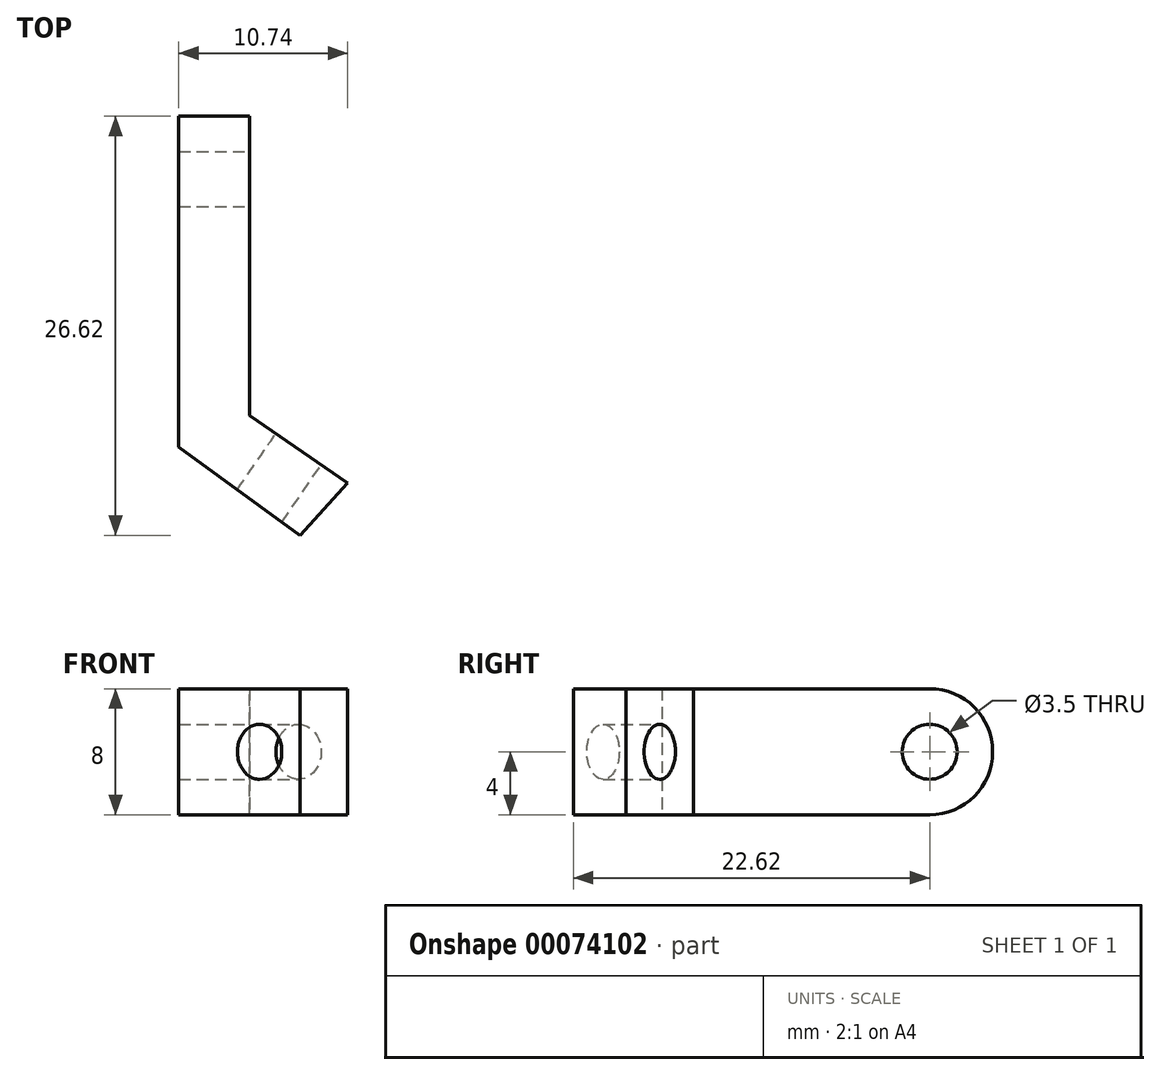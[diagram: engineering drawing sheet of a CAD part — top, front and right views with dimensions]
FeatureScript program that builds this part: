
annotation { "Feature Type Name" : "Feature", "Feature Type Description" : "" }
export const myFeature = defineFeature(function(context is Context, id is Id, definition is map)
    precondition{}
    {
        {
            var Q0;
            Q0=qCreatedBy(makeId("Top.planeOp"),FACE);
            var sketch = newSketch(context, id + "F0", { "sketchPlane" : qUnion([Q0])});
            skLineSegment(sketch, "E0", {"start": v(0, 0) * mm, "end": v(0, -21) * mm});
            skLineSegment(sketch, "E1", {"start": v(0, 0) * mm, "end": v(4.5, 0) * mm});
            skLineSegment(sketch, "E2", {"start": v(4.5, 0) * mm, "end": v(4.5, -19) * mm});
            skLineSegment(sketch, "E3", {"start": v(7.72, -26.62) * mm, "end": v(0, -21) * mm});
            skLineSegment(sketch, "E4", {"start": v(10.74, -23.28) * mm, "end": v(4.5, -19) * mm});
            skLineSegment(sketch, "E5", {"start": v(7.72, -26.62) * mm, "end": v(10.74, -23.28) * mm});
            skSolve(sketch);
        }
        {
            var Q0;
            Q0=makeQuery(id+"F0.imprint","IMPRINT",FACE,{"disambiguationData":[TD([[makeQuery(id+"F0.imprint","IMPRINT",EDGE,{"derivedFrom":sQuery(id+"F0.wireOp",EDGE,"E0")}),1.0]])]});
            var Q1;
            {var subQ3=sQuery(id+"F0.wireOp",EDGE,"l58EZqPc-FLeH-wLxH-H9D7-pOg8m8mRtfT9");Q1=makeQuery(id+"F0.imprint","IMPRINT",FACE,{"disambiguationData":[TD([[makeQuery(id+"F0.imprint","IMPRINT",EDGE,{"derivedFrom":subQ3}),-1.0]])]});}
            extrude(context, id + "F1", {"entities" : qUnion([Q0, Q1]), "depth" : 8 * mm});
        }
        {
            var Q0;
            Q0=makeQuery(id+"F1.opExtrude","CAP_EDGE",EDGE,{"disambiguationData":[OSD([sQuery(id+"F0.wireOp",EDGE,"E1")])],"isStart":false});
            var Q1;
            Q1=makeQuery(id+"F1.opExtrude","CAP_EDGE",EDGE,{"disambiguationData":[OSD([sQuery(id+"F0.wireOp",EDGE,"E1")])],"isStart":true});
            var Q2;
            Q2=makeQuery(id+"F1.opExtrude","CAP_EDGE",EDGE,{"disambiguationData":[OSD([sQuery(id+"F0.wireOp",EDGE,"EgyDUQFE-vDOO-uSj2-E7Fw-uX1ybdiR7PVY")])],"isStart":false});
            var Q3;
            Q3=makeQuery(id+"F1.opExtrude","CAP_EDGE",EDGE,{"disambiguationData":[OSD([sQuery(id+"F0.wireOp",EDGE,"EgyDUQFE-vDOO-uSj2-E7Fw-uX1ybdiR7PVY")])],"isStart":true});
            fillet(context, id + "F2", {"entities" : qUnion([Q0, Q1, Q2, Q3]), "radius" : 4 * mm, "tangentPropagation" : true, "allowEdgeOverflow" : false});
        }
        {
            var Q0;
            Q0=makeQuery(id+"F1.opExtrude","SWEPT_FACE",FACE,{"disambiguationData":[OSD([sQuery(id+"F0.wireOp",EDGE,"E2")])]});
            var sketch = newSketch(context, id + "F3", { "sketchPlane" : qUnion([Q0])});
            skCircle(sketch, "E6", {"center": v(-4, 4) * mm, "radius": 1.75 * mm});
            skSolve(sketch);
        }
        {
            var Q0;
            Q0=makeQuery(id+"F3.imprint","IMPRINT",FACE,{"disambiguationData":[TD([[makeQuery(id+"F3.imprint","IMPRINT",EDGE,{"derivedFrom":sQuery(id+"F3.wireOp",EDGE,"E6")}),1.0]])]});
            extrude(context, id + "F4", {"entities" : qUnion([Q0]), "operationType" : NewBodyOperationType.REMOVE, "oppositeDirection" : true, "depth" : 4.5 * mm});
        }
        {
            var Q0;
            Q0=makeQuery(id+"F1.opExtrude","SWEPT_FACE",FACE,{"disambiguationData":[OSD([sQuery(id+"F0.wireOp",EDGE,"E4")])]});
            var sketch = newSketch(context, id + "F5", { "sketchPlane" : qUnion([Q0])});
            skCircle(sketch, "E7", {"center": v(-18.25, 4) * mm, "radius": 1.75 * mm});
            skSolve(sketch);
        }
        {
            var Q0;
            Q0=makeQuery(id+"F5.imprint","IMPRINT",FACE,{"disambiguationData":[TD([[makeQuery(id+"F5.imprint","IMPRINT",EDGE,{"derivedFrom":sQuery(id+"F5.wireOp",EDGE,"E7")}),1.0]])]});
            extrude(context, id + "F6", {"entities" : qUnion([Q0]), "operationType" : NewBodyOperationType.REMOVE, "oppositeDirection" : true, "depth" : 4.84 * mm});
        }
    });
